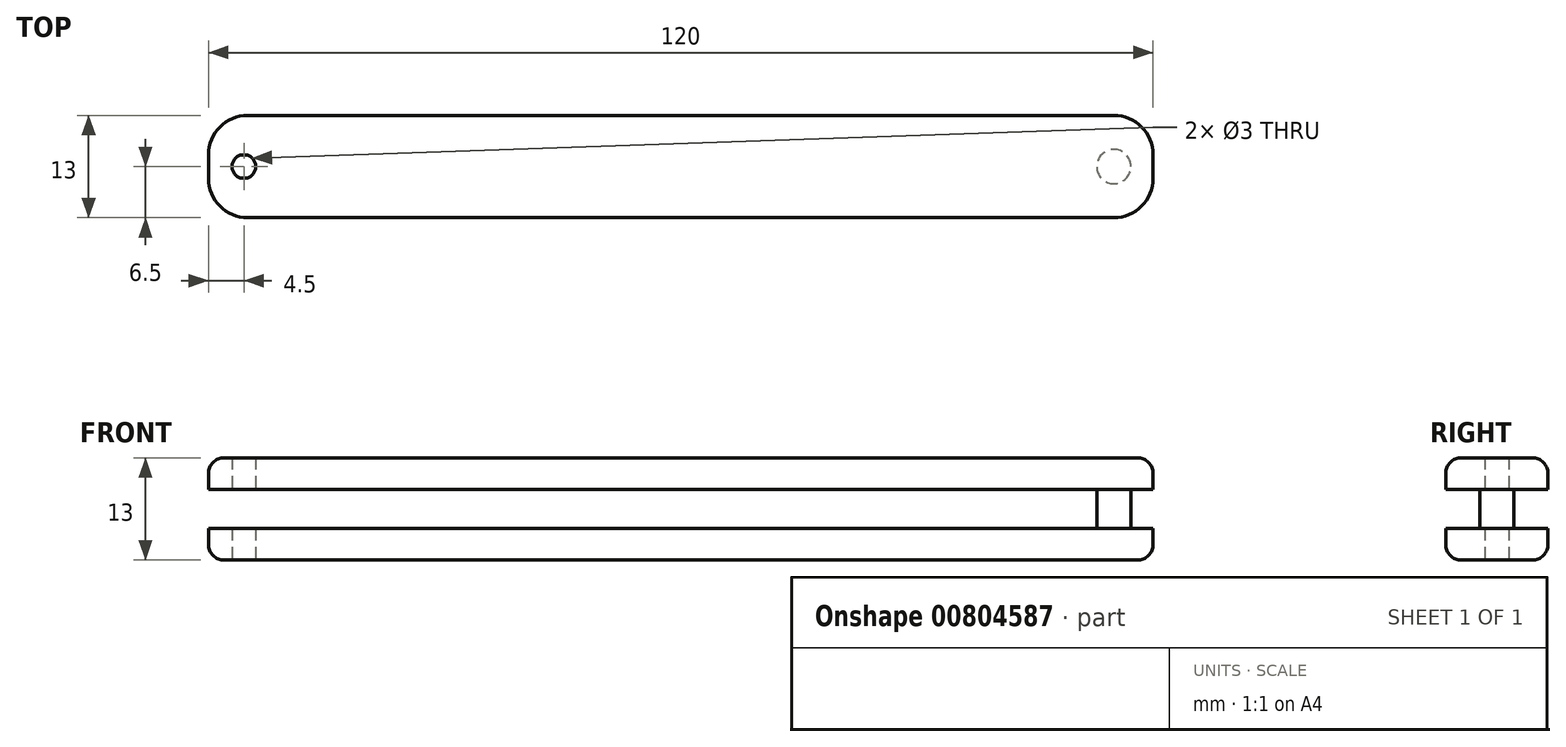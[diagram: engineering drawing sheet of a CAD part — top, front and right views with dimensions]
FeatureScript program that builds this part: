
annotation { "Feature Type Name" : "Feature", "Feature Type Description" : "" }
export const myFeature = defineFeature(function(context is Context, id is Id, definition is map)
    precondition{}
    {
        {
            var Q0;
            Q0=qCreatedBy(makeId("Top.planeOp"),FACE);
            var sketch = newSketch(context, id + "F0", { "sketchPlane" : qUnion([Q0])});
            skLineSegment(sketch, "E0.rect.bottom", {"start": v(60, 6.5) * mm, "end": v(-60, 6.5) * mm});
            skLineSegment(sketch, "E0.rect.top", {"start": v(60, -6.5) * mm, "end": v(-60, -6.5) * mm});
            skLineSegment(sketch, "E0.rect.left", {"start": v(60, 6.5) * mm, "end": v(60, -6.5) * mm});
            skLineSegment(sketch, "E0.rect.right", {"start": v(-60, 6.5) * mm, "end": v(-60, -6.5) * mm});
            skPoint(sketch, "E0.rect.middle", {"position": v(0, 0) * mm});
            skLineSegment(sketch, "E1", {"start": v(0, 6.5) * mm, "end": v(0, -6.5) * mm, "construction": true});
            skLineSegment(sketch, "E2", {"start": v(-60, 0) * mm, "end": v(60, 0) * mm, "construction": true});
            skLineSegment(sketch, "E3", {"start": v(-60, 0) * mm, "end": v(-55.5, 0) * mm, "construction": true});
            skCircle(sketch, "E4", {"center": v(-55.5, 0) * mm, "radius": 1.5 * mm});
            skLineSegment(sketch, "E5", {"start": v(60, 0) * mm, "end": v(55, 0) * mm, "construction": true});
            skSolve(sketch);
        }
        {
            var Q0;
            Q0=qSketchRegion(id+"F0",true);
            extrude(context, id + "F1", {"entities" : qUnion([Q0]), "depth" : 13 * mm});
        }
        {
            var Q0;
            Q0=qCreatedBy(makeId("Front.planeOp"),FACE);
            var sketch = newSketch(context, id + "F2", { "sketchPlane" : qUnion([Q0])});
            skLineSegment(sketch, "E6", {"start": v(0, 0) * mm, "end": v(0, 13) * mm, "construction": true});
            skLineSegment(sketch, "E7.rect.bottom", {"start": v(60, 9) * mm, "end": v(-60, 9) * mm});
            skLineSegment(sketch, "E7.rect.top", {"start": v(60, 4) * mm, "end": v(-60, 4) * mm});
            skLineSegment(sketch, "E7.rect.left", {"start": v(60, 9) * mm, "end": v(60, 4) * mm});
            skLineSegment(sketch, "E7.rect.right", {"start": v(-60, 9) * mm, "end": v(-60, 4) * mm});
            skPoint(sketch, "E7.rect.middle", {"position": v(0, 6.5) * mm});
            skSolve(sketch);
        }
        {
            var Q0;
            Q0=makeQuery(id+"F2.imprint","IMPRINT",FACE,{"disambiguationData":[TD([[makeQuery(id+"F2.imprint","IMPRINT",EDGE,{"derivedFrom":sQuery(id+"F2.wireOp",EDGE,"E7.rect.bottom")}),1.0]])]});
            extrude(context, id + "F3", {"entities" : qUnion([Q0]), "operationType" : NewBodyOperationType.REMOVE, "oppositeDirection" : true, "depth" : 8 * mm, "hasSecondDirection" : true, "secondDirectionOppositeDirection" : false, "secondDirectionDepth" : 8 * mm});
        }
        {
            var Q0;
            Q0=qCreatedBy(makeId("Top.planeOp"),FACE);
            var sketch = newSketch(context, id + "F4", { "sketchPlane" : qUnion([Q0])});
            skCircle(sketch, "E8", {"center": v(55.01, 0) * mm, "radius": 2.17 * mm});
            skSolve(sketch);
        }
        {
            var Q0;
            Q0=qSketchRegion(id+"F4",true);
            extrude(context, id + "F5", {"entities" : qUnion([Q0]), "operationType" : NewBodyOperationType.ADD, "depth" : 13 * mm});
        }
        {
            var Q0;
            Q0=makeQuery(id+"F1.opExtrude","CAP_EDGE",EDGE,{"disambiguationData":[OSD([sQuery(id+"F0.wireOp",EDGE,"E0.rect.top")])],"isStart":false});
            var Q1;
            Q1=makeQuery(id+"F1.opExtrude","CAP_EDGE",EDGE,{"disambiguationData":[OSD([sQuery(id+"F0.wireOp",EDGE,"E0.rect.right")])],"isStart":false});
            var Q2;
            Q2=makeQuery(id+"F1.opExtrude","CAP_EDGE",EDGE,{"disambiguationData":[OSD([sQuery(id+"F0.wireOp",EDGE,"E0.rect.bottom")])],"isStart":false});
            var Q3;
            Q3=makeQuery(id+"F1.opExtrude","CAP_EDGE",EDGE,{"disambiguationData":[OSD([sQuery(id+"F0.wireOp",EDGE,"E0.rect.left")])],"isStart":false});
            var Q4;
            Q4=makeQuery(id+"F1.opExtrude","CAP_EDGE",EDGE,{"disambiguationData":[OSD([sQuery(id+"F0.wireOp",EDGE,"E0.rect.right")])],"isStart":true});
            var Q5;
            Q5=makeQuery(id+"F1.opExtrude","CAP_EDGE",EDGE,{"disambiguationData":[OSD([sQuery(id+"F0.wireOp",EDGE,"E0.rect.top")])],"isStart":true});
            var Q6;
            Q6=makeQuery(id+"F1.opExtrude","CAP_EDGE",EDGE,{"disambiguationData":[OSD([sQuery(id+"F0.wireOp",EDGE,"E0.rect.left")])],"isStart":true});
            var Q7;
            Q7=makeQuery(id+"F1.opExtrude","CAP_EDGE",EDGE,{"disambiguationData":[OSD([sQuery(id+"F0.wireOp",EDGE,"E0.rect.bottom")])],"isStart":true});
            fillet(context, id + "F6", {"entities" : qUnion([Q0, Q1, Q2, Q3, Q4, Q5, Q6, Q7]), "radius" : 2 * mm, "tangentPropagation" : true, "allowEdgeOverflow" : false});
        }
        {
            var Q0;
            {var subQ0=sQuery(id+"F0.wireOp",EDGE,"E0.rect.top");var subQ1=sQuery(id+"F0.wireOp",EDGE,"E0.rect.right");Q0=makeQuery(id+"F3.boolean.opBoolean","SPLIT",EDGE,{"disambiguationData":[TD([makeQuery(id+"F3.opExtrude","SWEPT_FACE",FACE,{"disambiguationData":[OSD([sQuery(id+"F2.wireOp",EDGE,"E7.rect.bottom")])]})])],"derivedFrom":makeQuery(id+"F1.opExtrude","SWEPT_EDGE",EDGE,{"disambiguationData":[OSD([subQ0,subQ1])]})});}
            var Q1;
            {var subQ0=sQuery(id+"F0.wireOp",EDGE,"E0.rect.bottom");var subQ1=sQuery(id+"F0.wireOp",EDGE,"E0.rect.right");Q1=makeQuery(id+"F3.boolean.opBoolean","SPLIT",EDGE,{"disambiguationData":[TD([makeQuery(id+"F3.opExtrude","SWEPT_FACE",FACE,{"disambiguationData":[OSD([sQuery(id+"F2.wireOp",EDGE,"E7.rect.bottom")])]})])],"derivedFrom":makeQuery(id+"F1.opExtrude","SWEPT_EDGE",EDGE,{"disambiguationData":[OSD([subQ0,subQ1])]})});}
            var Q2;
            {var subQ0=sQuery(id+"F0.wireOp",EDGE,"E0.rect.top");var subQ1=sQuery(id+"F0.wireOp",EDGE,"E0.rect.right");Q2=makeQuery(id+"F3.boolean.opBoolean","SPLIT",EDGE,{"disambiguationData":[TD([makeQuery(id+"F3.opExtrude","SWEPT_FACE",FACE,{"disambiguationData":[OSD([sQuery(id+"F2.wireOp",EDGE,"E7.rect.top")])]})])],"derivedFrom":makeQuery(id+"F1.opExtrude","SWEPT_EDGE",EDGE,{"disambiguationData":[OSD([subQ0,subQ1])]})});}
            var Q3;
            {var subQ0=sQuery(id+"F0.wireOp",EDGE,"E0.rect.bottom");var subQ1=sQuery(id+"F0.wireOp",EDGE,"E0.rect.right");Q3=makeQuery(id+"F3.boolean.opBoolean","SPLIT",EDGE,{"disambiguationData":[TD([makeQuery(id+"F3.opExtrude","SWEPT_FACE",FACE,{"disambiguationData":[OSD([sQuery(id+"F2.wireOp",EDGE,"E7.rect.top")])]})])],"derivedFrom":makeQuery(id+"F1.opExtrude","SWEPT_EDGE",EDGE,{"disambiguationData":[OSD([subQ0,subQ1])]})});}
            var Q4;
            {var subQ0=sQuery(id+"F0.wireOp",EDGE,"E0.rect.top");var subQ1=sQuery(id+"F0.wireOp",EDGE,"E0.rect.left");Q4=makeQuery(id+"F3.boolean.opBoolean","SPLIT",EDGE,{"disambiguationData":[TD([makeQuery(id+"F3.opExtrude","SWEPT_FACE",FACE,{"disambiguationData":[OSD([sQuery(id+"F2.wireOp",EDGE,"E7.rect.bottom")])]})])],"derivedFrom":makeQuery(id+"F1.opExtrude","SWEPT_EDGE",EDGE,{"disambiguationData":[OSD([subQ0,subQ1])]})});}
            var Q5;
            {var subQ0=sQuery(id+"F0.wireOp",EDGE,"E0.rect.bottom");var subQ1=sQuery(id+"F0.wireOp",EDGE,"E0.rect.left");Q5=makeQuery(id+"F3.boolean.opBoolean","SPLIT",EDGE,{"disambiguationData":[TD([makeQuery(id+"F3.opExtrude","SWEPT_FACE",FACE,{"disambiguationData":[OSD([sQuery(id+"F2.wireOp",EDGE,"E7.rect.bottom")])]})])],"derivedFrom":makeQuery(id+"F1.opExtrude","SWEPT_EDGE",EDGE,{"disambiguationData":[OSD([subQ0,subQ1])]})});}
            var Q6;
            {var subQ0=sQuery(id+"F0.wireOp",EDGE,"E0.rect.top");var subQ1=sQuery(id+"F0.wireOp",EDGE,"E0.rect.left");Q6=makeQuery(id+"F3.boolean.opBoolean","SPLIT",EDGE,{"disambiguationData":[TD([makeQuery(id+"F3.opExtrude","SWEPT_FACE",FACE,{"disambiguationData":[OSD([sQuery(id+"F2.wireOp",EDGE,"E7.rect.top")])]})])],"derivedFrom":makeQuery(id+"F1.opExtrude","SWEPT_EDGE",EDGE,{"disambiguationData":[OSD([subQ0,subQ1])]})});}
            var Q7;
            {var subQ0=sQuery(id+"F0.wireOp",EDGE,"E0.rect.bottom");var subQ1=sQuery(id+"F0.wireOp",EDGE,"E0.rect.left");Q7=makeQuery(id+"F3.boolean.opBoolean","SPLIT",EDGE,{"disambiguationData":[TD([makeQuery(id+"F3.opExtrude","SWEPT_FACE",FACE,{"disambiguationData":[OSD([sQuery(id+"F2.wireOp",EDGE,"E7.rect.top")])]})])],"derivedFrom":makeQuery(id+"F1.opExtrude","SWEPT_EDGE",EDGE,{"disambiguationData":[OSD([subQ0,subQ1])]})});}
            fillet(context, id + "F7", {"entities" : qUnion([Q0, Q1, Q2, Q3, Q4, Q5, Q6, Q7]), "radius" : 5 * mm, "tangentPropagation" : true, "allowEdgeOverflow" : false});
        }
    });
